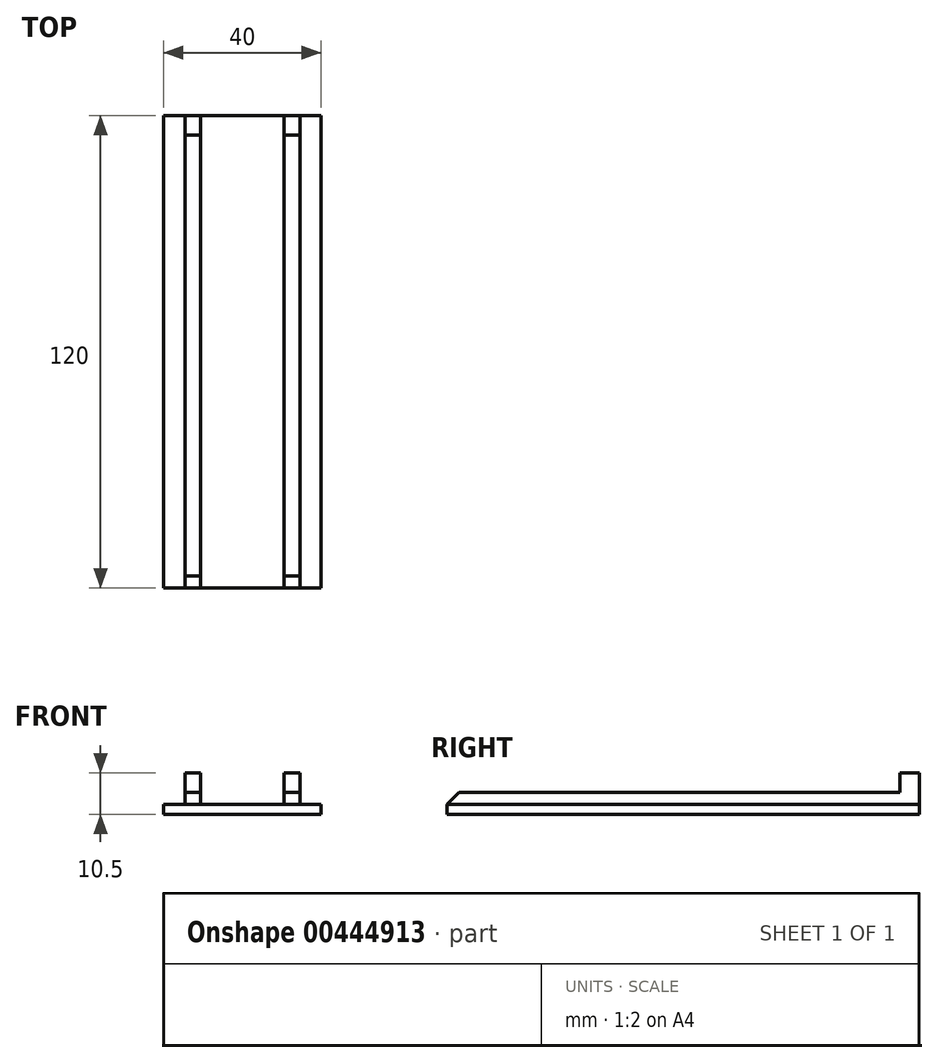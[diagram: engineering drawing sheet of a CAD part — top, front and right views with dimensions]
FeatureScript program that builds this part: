
annotation { "Feature Type Name" : "Feature", "Feature Type Description" : "" }
export const myFeature = defineFeature(function(context is Context, id is Id, definition is map)
    precondition{}
    {
        {
            var Q0;
            Q0=qCreatedBy(makeId("Top.planeOp"),FACE);
            var sketch = newSketch(context, id + "F0", { "sketchPlane" : qUnion([Q0])});
            skLineSegment(sketch, "E0.bottom", {"start": v(20, -60) * mm, "end": v(-20, -60) * mm});
            skLineSegment(sketch, "E0.top", {"start": v(20, 60) * mm, "end": v(-20, 60) * mm});
            skLineSegment(sketch, "E0.left", {"start": v(20, -60) * mm, "end": v(20, 60) * mm});
            skLineSegment(sketch, "E0.right", {"start": v(-20, -60) * mm, "end": v(-20, 60) * mm});
            skPoint(sketch, "E0.middle", {"position": v(0, 0) * mm});
            skSolve(sketch);
        }
        {
            var Q0;
            Q0 = qSketchRegion(id + "F0", true);
            extrude(context, id + "F1", {"entities" : qUnion([Q0]), "depth" : 2.5 * mm});
        }
        {
            var Q0;
            Q0=makeQuery(id+"F1.opExtrude","CAP_FACE",FACE,{"disambiguationData":[OSD([sQuery(id+"F0.wireOp",EDGE,"E0.bottom"),sQuery(id+"F0.wireOp",EDGE,"E0.top"),sQuery(id+"F0.wireOp",EDGE,"E0.left"),sQuery(id+"F0.wireOp",EDGE,"E0.right")])],"isStart":false});
            var sketch = newSketch(context, id + "F2", { "sketchPlane" : qUnion([Q0])});
            skLineSegment(sketch, "E1", {"start": v(-14.6, 60) * mm, "end": v(-14.6, -60) * mm});
            skLineSegment(sketch, "E2", {"start": v(-10.6, -60) * mm, "end": v(-10.6, 60) * mm});
            skLineSegment(sketch, "E3.MirrorCS", {"start": v(10.6, -60) * mm, "end": v(10.6, 60) * mm});
            skLineSegment(sketch, "E4.MirrorCS", {"start": v(14.6, 60) * mm, "end": v(14.6, -60) * mm});
            skSolve(sketch);
        }
        {
            var Q0;
            {var subQ0=sQuery(id+"F2.wireOp",EDGE,"E1");Q0=makeQuery(id+"F2.imprint","IMPRINT",FACE,{"disambiguationData":[TD([[makeQuery(id+"F2.imprint","IMPRINT",EDGE,{"derivedFrom":subQ0}),1.0]])]});}
            var Q1;
            {var subQ0=sQuery(id+"F2.wireOp",EDGE,"E3.MirrorCS");Q1=makeQuery(id+"F2.imprint","IMPRINT",FACE,{"disambiguationData":[TD([[makeQuery(id+"F2.imprint","IMPRINT",EDGE,{"derivedFrom":subQ0}),-1.0]])]});}
            extrude(context, id + "F3", {"entities" : qUnion([Q0, Q1]), "operationType" : NewBodyOperationType.ADD, "depth" : 3 * mm});
        }
        {
            var Q0;
            {var subQ0=sQuery(id+"F0.wireOp",EDGE,"E0.bottom");var subQ1=makeQuery(id+"F1.opExtrude","CAP_EDGE",EDGE,{"disambiguationData":[OSD([subQ0])],"isStart":false});Q0=makeQuery(id+"F3.opExtrude","CAP_EDGE",EDGE,{"disambiguationData":[OSD([subQ0]),TDD([makeQuery(id+"F2.imprint","IMPRINT",EDGE,{"disambiguationData":[TD([[makeQuery(id+"F2.imprint","INTERSECT",VERTEX,{"derivedFrom":[subQ1,sQuery(id+"F2.wireOp",EDGE,"E1")]}),1.0]])],"derivedFrom":subQ1})])],"isStart":false});}
            var Q1;
            {var subQ0=sQuery(id+"F0.wireOp",EDGE,"E0.bottom");var subQ1=makeQuery(id+"F1.opExtrude","CAP_EDGE",EDGE,{"disambiguationData":[OSD([subQ0])],"isStart":false});Q1=makeQuery(id+"F3.opExtrude","CAP_EDGE",EDGE,{"disambiguationData":[OSD([subQ0]),TDD([makeQuery(id+"F2.imprint","IMPRINT",EDGE,{"disambiguationData":[TD([[makeQuery(id+"F2.imprint","INTERSECT",VERTEX,{"derivedFrom":[subQ1,sQuery(id+"F2.wireOp",EDGE,"E3.MirrorCS")]}),1.0]])],"derivedFrom":subQ1})])],"isStart":false});}
            chamfer(context, id + "F4", {"entities" : qUnion([Q0, Q1]), "width" : 3 * mm, "tangentPropagation" : true});
        }
        {
            var Q0;
            Q0=makeQuery(id+"F3.opExtrude","CAP_FACE",FACE,{"disambiguationData":[OSD([sQuery(id+"F0.wireOp",EDGE,"E0.bottom"),sQuery(id+"F0.wireOp",EDGE,"E0.top"),sQuery(id+"F2.wireOp",EDGE,"E3.MirrorCS"),sQuery(id+"F2.wireOp",EDGE,"E4.MirrorCS")])],"isStart":false});
            var sketch = newSketch(context, id + "F5", { "sketchPlane" : qUnion([Q0])});
            skLineSegment(sketch, "E5", {"start": v(10.6, 55) * mm, "end": v(14.6, 55) * mm});
            skLineSegment(sketch, "E6", {"start": v(14.6, 55) * mm, "end": v(14.6, 60) * mm});
            skLineSegment(sketch, "E7", {"start": v(14.6, 60) * mm, "end": v(10.6, 60) * mm});
            skLineSegment(sketch, "E8", {"start": v(10.6, 60) * mm, "end": v(10.6, 55) * mm});
            skLineSegment(sketch, "E9.MirrorCS", {"start": v(-10.6, 60) * mm, "end": v(-10.6, 55) * mm});
            skLineSegment(sketch, "E10.MirrorCS", {"start": v(-10.6, 55) * mm, "end": v(-14.6, 55) * mm});
            skLineSegment(sketch, "E11.MirrorCS", {"start": v(-14.6, 55) * mm, "end": v(-14.6, 60) * mm});
            skLineSegment(sketch, "E12.MirrorCS", {"start": v(-14.6, 60) * mm, "end": v(-10.6, 60) * mm});
            skSolve(sketch);
        }
        {
            var Q0;
            Q0=makeQuery(id+"F5.imprint","IMPRINT",FACE,{"disambiguationData":[TD([[makeQuery(id+"F5.imprint","IMPRINT",EDGE,{"derivedFrom":sQuery(id+"F5.wireOp",EDGE,"E5")}),1.0]])]});
            var Q1;
            Q1=makeQuery(id+"F5.imprint","IMPRINT",FACE,{"disambiguationData":[TD([[makeQuery(id+"F5.imprint","IMPRINT",EDGE,{"derivedFrom":sQuery(id+"F5.wireOp",EDGE,"E9.MirrorCS")}),-1.0]])]});
            extrude(context, id + "F6", {"entities" : qUnion([Q0, Q1]), "operationType" : NewBodyOperationType.ADD, "depth" : 5 * mm});
        }
    });
